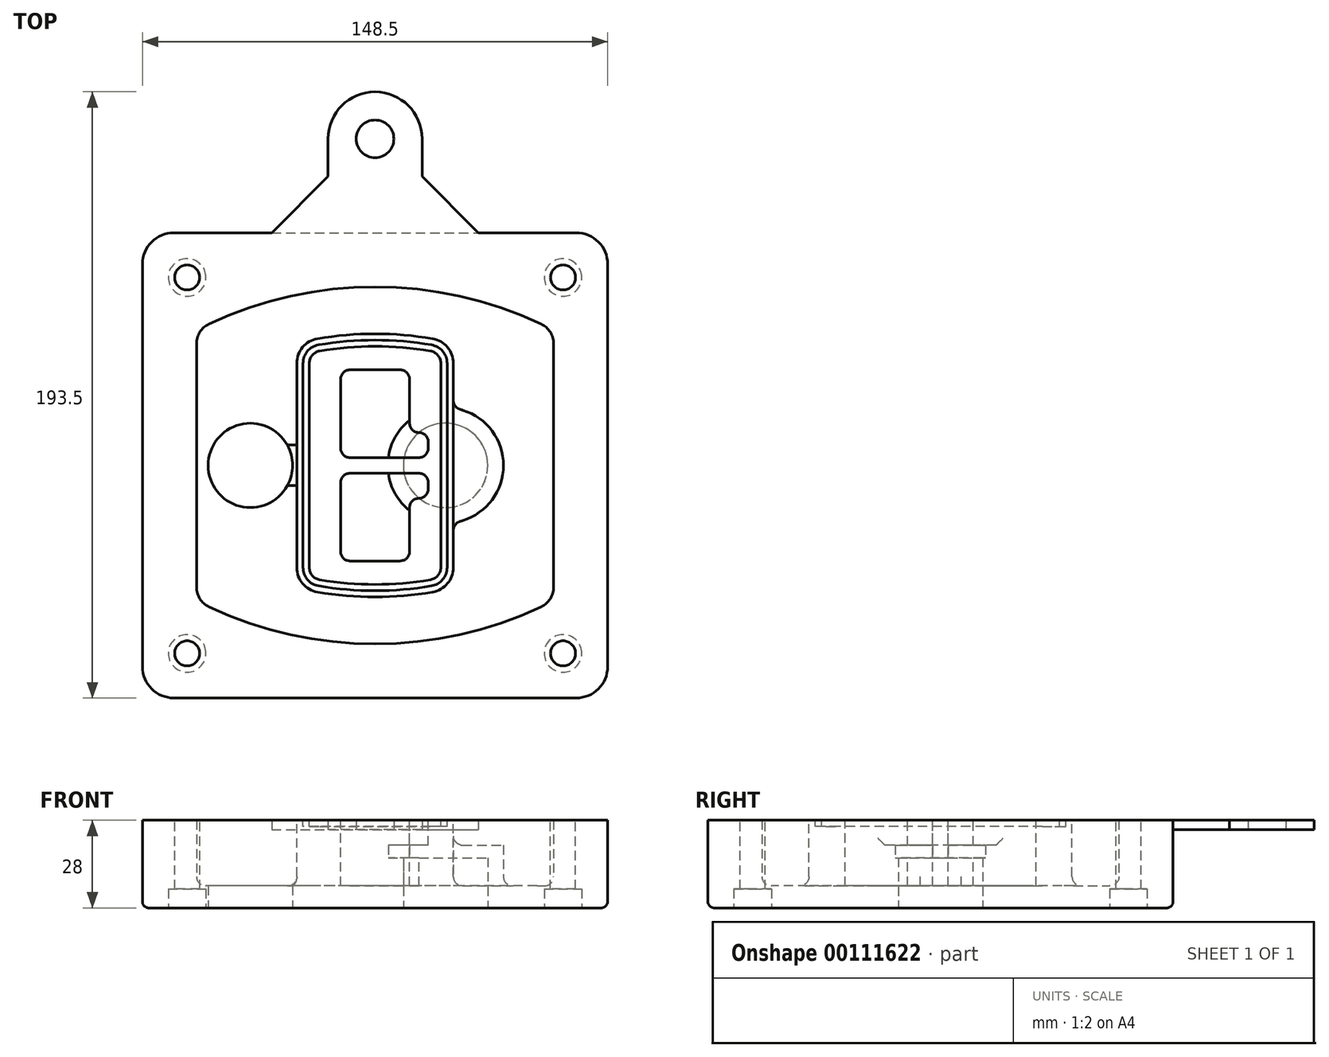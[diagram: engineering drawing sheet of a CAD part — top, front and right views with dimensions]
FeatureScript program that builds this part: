
annotation { "Feature Type Name" : "Feature", "Feature Type Description" : "" }
export const myFeature = defineFeature(function(context is Context, id is Id, definition is map)
    precondition{}
    {
        {
            var Q0;
            Q0=qCreatedBy(makeId("Top.planeOp"),FACE);
            var sketch = newSketch(context, id + "F0", { "sketchPlane" : qUnion([Q0])});
            skPoint(sketch, "E0.rect.middle", {"position": v(0, 0) * mm});
            skLineSegment(sketch, "E1.bottom", {"start": v(-64.25, -74.25) * mm, "end": v(64.25, -74.25) * mm});
            skLineSegment(sketch, "E1.top", {"start": v(-64.25, 74.25) * mm, "end": v(64.25, 74.25) * mm});
            skLineSegment(sketch, "E1.left", {"start": v(-74.25, -64.25) * mm, "end": v(-74.25, 64.25) * mm});
            skLineSegment(sketch, "E1.right", {"start": v(74.25, -64.25) * mm, "end": v(74.25, 64.25) * mm});
            skLineSegment(sketch, "E2", {"start": v(-74.25, 74.25) * mm, "end": v(74.25, -74.25) * mm, "construction": true});
            skLineSegment(sketch, "E3", {"start": v(74.25, 74.25) * mm, "end": v(-74.25, -74.25) * mm, "construction": true});
            skCircle(sketch, "E4", {"center": v(-60, 60) * mm, "radius": 4 * mm});
            skCircle(sketch, "E5", {"center": v(60, 60) * mm, "radius": 4 * mm});
            skCircle(sketch, "E6", {"center": v(60, -60) * mm, "radius": 4 * mm});
            skCircle(sketch, "E7", {"center": v(-60, -60) * mm, "radius": 4 * mm});
            skLineSegment(sketch, "E8", {"start": v(-60, 60) * mm, "end": v(60, 60) * mm, "construction": true});
            skLineSegment(sketch, "E9", {"start": v(60, 60) * mm, "end": v(60, -60) * mm, "construction": true});
            skLineSegment(sketch, "E10", {"start": v(60, -60) * mm, "end": v(-60, -60) * mm, "construction": true});
            skLineSegment(sketch, "E11", {"start": v(-60, -60) * mm, "end": v(-60, 60) * mm, "construction": true});
            skLineSegment(sketch, "E12", {"start": v(-60, 38.83) * mm, "end": v(-60, -38.83) * mm});
            skLineSegment(sketch, "E13", {"start": v(60, 38.83) * mm, "end": v(60, -38.83) * mm});
            skArc(sketch, "E14", {"start": v(54.26, 47.88) * mm, "mid": v(0, 60) * mm, "end": v(-54.26, 47.88) * mm});
            skArc(sketch, "E15", {"start": v(-54.26, -47.88) * mm, "mid": v(0, -60) * mm, "end": v(54.26, -47.88) * mm});
            skLineSegment(sketch, "E16", {"start": v(-60, 0) * mm, "end": v(60, 0) * mm, "construction": true});
            skPoint(sketch, "E17.visualSharp", {"position": v(-60, -45) * mm});
            skArc(sketch, "E17.filletArc", {"start": v(-60, -38.83) * mm, "mid": v(-58.44, -44.2) * mm, "end": v(-54.26, -47.88) * mm});
            skPoint(sketch, "E18.visualSharp", {"position": v(-60, 45) * mm});
            skArc(sketch, "E18.filletArc", {"start": v(-54.26, 47.88) * mm, "mid": v(-58.44, 44.2) * mm, "end": v(-60, 38.83) * mm});
            skPoint(sketch, "E19.visualSharp", {"position": v(60, 45) * mm});
            skArc(sketch, "E19.filletArc", {"start": v(60, 38.83) * mm, "mid": v(58.44, 44.2) * mm, "end": v(54.26, 47.88) * mm});
            skPoint(sketch, "E20.visualSharp", {"position": v(60, -45) * mm});
            skArc(sketch, "E20.filletArc", {"start": v(54.26, -47.88) * mm, "mid": v(58.44, -44.2) * mm, "end": v(60, -38.83) * mm});
            skPoint(sketch, "E21.visualSharp", {"position": v(-74.25, 74.25) * mm});
            skArc(sketch, "E21.filletArc", {"start": v(-64.25, 74.25) * mm, "mid": v(-71.32, 71.32) * mm, "end": v(-74.25, 64.25) * mm});
            skPoint(sketch, "E22.visualSharp", {"position": v(74.25, 74.25) * mm});
            skArc(sketch, "E22.filletArc", {"start": v(74.25, 64.25) * mm, "mid": v(71.32, 71.32) * mm, "end": v(64.25, 74.25) * mm});
            skPoint(sketch, "E23.visualSharp", {"position": v(74.25, -74.25) * mm});
            skArc(sketch, "E23.filletArc", {"start": v(64.25, -74.25) * mm, "mid": v(71.32, -71.32) * mm, "end": v(74.25, -64.25) * mm});
            skPoint(sketch, "E24.visualSharp", {"position": v(-74.25, -74.25) * mm});
            skArc(sketch, "E24.filletArc", {"start": v(-74.25, -64.25) * mm, "mid": v(-71.32, -71.32) * mm, "end": v(-64.25, -74.25) * mm});
            skArc(sketch, "E25.0", {"start": v(57, 38.83) * mm, "mid": v(55.9, 42.58) * mm, "end": v(52.98, 45.17) * mm});
            skLineSegment(sketch, "E25.1", {"start": v(57, 38.83) * mm, "end": v(57, -38.83) * mm});
            skArc(sketch, "E25.2", {"start": v(52.98, -45.17) * mm, "mid": v(55.9, -42.58) * mm, "end": v(57, -38.83) * mm});
            skArc(sketch, "E25.3", {"start": v(-52.98, -45.17) * mm, "mid": v(0, -57) * mm, "end": v(52.98, -45.17) * mm});
            skArc(sketch, "E25.4", {"start": v(-57, -38.83) * mm, "mid": v(-55.9, -42.58) * mm, "end": v(-52.98, -45.17) * mm});
            skArc(sketch, "E25.5", {"start": v(52.98, 45.17) * mm, "mid": v(0, 57) * mm, "end": v(-52.98, 45.17) * mm});
            skLineSegment(sketch, "E25.6", {"start": v(-57, 38.83) * mm, "end": v(-57, -38.83) * mm});
            skArc(sketch, "E25.7", {"start": v(-52.98, 45.17) * mm, "mid": v(-55.9, 42.58) * mm, "end": v(-57, 38.83) * mm});
            skArc(sketch, "E26.0", {"start": v(-55.96, 51.5) * mm, "mid": v(-61.82, 46.33) * mm, "end": v(-64, 38.83) * mm});
            skArc(sketch, "E26.1", {"start": v(55.96, 51.5) * mm, "mid": v(0, 64) * mm, "end": v(-55.96, 51.5) * mm});
            skArc(sketch, "E26.2", {"start": v(64, 38.83) * mm, "mid": v(61.82, 46.33) * mm, "end": v(55.96, 51.5) * mm});
            skLineSegment(sketch, "E26.3", {"start": v(64, 38.83) * mm, "end": v(64, -38.83) * mm});
            skArc(sketch, "E26.4", {"start": v(55.96, -51.5) * mm, "mid": v(61.82, -46.33) * mm, "end": v(64, -38.83) * mm});
            skLineSegment(sketch, "E26.5", {"start": v(-64, 38.83) * mm, "end": v(-64, -38.83) * mm});
            skArc(sketch, "E26.6", {"start": v(-55.96, -51.5) * mm, "mid": v(0, -64) * mm, "end": v(55.96, -51.5) * mm});
            skArc(sketch, "E26.7", {"start": v(-64, -38.83) * mm, "mid": v(-61.82, -46.33) * mm, "end": v(-55.96, -51.5) * mm});
            skSolve(sketch);
        }
        {
            var Q0;
            Q0=makeQuery(id+"F0.imprint","IMPRINT",FACE,{"disambiguationData":[TD([[makeQuery(id+"F0.imprint","IMPRINT",EDGE,{"derivedFrom":sQuery(id+"F0.wireOp",EDGE,"E1.bottom")}),1.0]])]});
            var Q1;
            Q1=makeQuery(id+"F0.imprint","IMPRINT",FACE,{"disambiguationData":[TD([[makeQuery(id+"F0.imprint","IMPRINT",EDGE,{"derivedFrom":sQuery(id+"F0.wireOp",EDGE,"E12")}),1.0]])]});
            var Q2;
            Q2=makeQuery(id+"F0.imprint","IMPRINT",FACE,{"disambiguationData":[TD([[makeQuery(id+"F0.imprint","IMPRINT",EDGE,{"derivedFrom":sQuery(id+"F0.wireOp",EDGE,"E25.0")}),1.0]])]});
            var Q3;
            Q3=makeQuery(id+"F0.imprint","IMPRINT",FACE,{"disambiguationData":[TD([[makeQuery(id+"F0.imprint","IMPRINT",EDGE,{"derivedFrom":sQuery(id+"F0.wireOp",EDGE,"E12")}),-1.0]])]});
            extrude(context, id + "F1", {"entities" : qUnion([Q0, Q1, Q2, Q3]), "oppositeDirection" : true, "depth" : 25 * mm});
        }
        {
            var Q0;
            Q0=makeQuery(id+"F0.imprint","IMPRINT",FACE,{"disambiguationData":[TD([[makeQuery(id+"F0.imprint","IMPRINT",EDGE,{"derivedFrom":sQuery(id+"F0.wireOp",EDGE,"E12")}),1.0]])]});
            extrude(context, id + "F2", {"entities" : qUnion([Q0]), "operationType" : NewBodyOperationType.ADD, "depth" : 3 * mm});
        }
        {
            var Q0;
            Q0=makeQuery(id+"F0.imprint","IMPRINT",FACE,{"disambiguationData":[TD([[makeQuery(id+"F0.imprint","IMPRINT",EDGE,{"derivedFrom":sQuery(id+"F0.wireOp",EDGE,"E25.0")}),1.0]])]});
            extrude(context, id + "F3", {"entities" : qUnion([Q0]), "operationType" : NewBodyOperationType.REMOVE, "oppositeDirection" : true, "depth" : 18 * mm});
        }
        {
            var Q0;
            Q0=makeQuery(id+"F2.opExtrude","CAP_FACE",FACE,{"disambiguationData":[OSD([sQuery(id+"F0.wireOp",EDGE,"E12"),sQuery(id+"F0.wireOp",EDGE,"E13"),sQuery(id+"F0.wireOp",EDGE,"E14"),sQuery(id+"F0.wireOp",EDGE,"E15"),sQuery(id+"F0.wireOp",EDGE,"E17.filletArc"),sQuery(id+"F0.wireOp",EDGE,"E18.filletArc"),sQuery(id+"F0.wireOp",EDGE,"E19.filletArc"),sQuery(id+"F0.wireOp",EDGE,"E20.filletArc"),sQuery(id+"F0.wireOp",EDGE,"E25.0"),sQuery(id+"F0.wireOp",EDGE,"E25.1"),sQuery(id+"F0.wireOp",EDGE,"E25.2"),sQuery(id+"F0.wireOp",EDGE,"E25.3"),sQuery(id+"F0.wireOp",EDGE,"E25.4"),sQuery(id+"F0.wireOp",EDGE,"E25.5"),sQuery(id+"F0.wireOp",EDGE,"E25.6"),sQuery(id+"F0.wireOp",EDGE,"E25.7")])],"isStart":false});
            var sketch = newSketch(context, id + "F4", { "sketchPlane" : qUnion([Q0])});
            skArc(sketch, "E27.0", {"start": v(-18.34, -40.45) * mm, "mid": v(0, -42) * mm, "end": v(18.34, -40.45) * mm});
            skArc(sketch, "E28.0", {"start": v(18.34, 40.45) * mm, "mid": v(0, 42) * mm, "end": v(-18.34, 40.45) * mm});
            skLineSegment(sketch, "E29", {"start": v(-25, 32.57) * mm, "end": v(-25, -32.57) * mm});
            skLineSegment(sketch, "E30", {"start": v(25, 32.57) * mm, "end": v(25, -32.57) * mm});
            skLineSegment(sketch, "E31", {"start": v(-25, 39.1) * mm, "end": v(25, 39.1) * mm, "construction": true});
            skLineSegment(sketch, "E32", {"start": v(-25, -39.1) * mm, "end": v(25, -39.1) * mm, "construction": true});
            skPoint(sketch, "E33.visualSharp", {"position": v(-25, 39.1) * mm});
            skArc(sketch, "E33.filletArc", {"start": v(-18.34, 40.45) * mm, "mid": v(-23.11, 37.73) * mm, "end": v(-25, 32.57) * mm});
            skPoint(sketch, "E34.visualSharp", {"position": v(25, 39.1) * mm});
            skArc(sketch, "E34.filletArc", {"start": v(25, 32.57) * mm, "mid": v(23.11, 37.73) * mm, "end": v(18.34, 40.45) * mm});
            skPoint(sketch, "E35.visualSharp", {"position": v(25, -39.1) * mm});
            skArc(sketch, "E35.filletArc", {"start": v(18.34, -40.45) * mm, "mid": v(23.11, -37.73) * mm, "end": v(25, -32.57) * mm});
            skPoint(sketch, "E36.visualSharp", {"position": v(-25, -39.1) * mm});
            skArc(sketch, "E36.filletArc", {"start": v(-25, -32.57) * mm, "mid": v(-23.11, -37.73) * mm, "end": v(-18.34, -40.45) * mm});
            skArc(sketch, "E37.0", {"start": v(52.98, 45.17) * mm, "mid": v(0, 57) * mm, "end": v(-52.98, 45.17) * mm});
            skArc(sketch, "E37.1", {"start": v(-52.98, 45.17) * mm, "mid": v(-55.9, 42.58) * mm, "end": v(-57, 38.83) * mm});
            skLineSegment(sketch, "E37.2", {"start": v(-57, 38.83) * mm, "end": v(-57, -38.83) * mm});
            skArc(sketch, "E37.3", {"start": v(-57, -38.83) * mm, "mid": v(-55.9, -42.58) * mm, "end": v(-52.98, -45.17) * mm});
            skArc(sketch, "E37.4", {"start": v(-52.98, -45.17) * mm, "mid": v(0, -57) * mm, "end": v(52.98, -45.17) * mm});
            skArc(sketch, "E37.5", {"start": v(52.98, -45.17) * mm, "mid": v(55.9, -42.58) * mm, "end": v(57, -38.83) * mm});
            skLineSegment(sketch, "E37.6", {"start": v(57, 38.83) * mm, "end": v(57, -38.83) * mm});
            skArc(sketch, "E37.7", {"start": v(57, 38.83) * mm, "mid": v(55.9, 42.58) * mm, "end": v(52.98, 45.17) * mm});
            skLineSegment(sketch, "E38.0", {"start": v(23, 32.57) * mm, "end": v(23, -32.57) * mm});
            skArc(sketch, "E38.1", {"start": v(18, -38.48) * mm, "mid": v(21.58, -36.44) * mm, "end": v(23, -32.57) * mm});
            skArc(sketch, "E38.2", {"start": v(-18, -38.48) * mm, "mid": v(0, -40) * mm, "end": v(18, -38.48) * mm});
            skArc(sketch, "E38.3", {"start": v(-23, -32.57) * mm, "mid": v(-21.58, -36.44) * mm, "end": v(-18, -38.48) * mm});
            skLineSegment(sketch, "E38.4", {"start": v(-23, 32.57) * mm, "end": v(-23, -32.57) * mm});
            skArc(sketch, "E38.5", {"start": v(23, 32.57) * mm, "mid": v(21.58, 36.44) * mm, "end": v(18, 38.48) * mm});
            skArc(sketch, "E38.6", {"start": v(-18, 38.48) * mm, "mid": v(-21.58, 36.44) * mm, "end": v(-23, 32.57) * mm});
            skArc(sketch, "E38.7", {"start": v(18, 38.48) * mm, "mid": v(0, 40) * mm, "end": v(-18, 38.48) * mm});
            skArc(sketch, "E39.0", {"start": v(21, 32.57) * mm, "mid": v(20.06, 35.15) * mm, "end": v(17.67, 36.5) * mm});
            skLineSegment(sketch, "E39.1", {"start": v(21, 32.57) * mm, "end": v(21, -32.57) * mm});
            skArc(sketch, "E39.2", {"start": v(17.67, -36.5) * mm, "mid": v(20.06, -35.15) * mm, "end": v(21, -32.57) * mm});
            skArc(sketch, "E39.3", {"start": v(-17.67, -36.5) * mm, "mid": v(0, -38) * mm, "end": v(17.67, -36.5) * mm});
            skArc(sketch, "E39.4", {"start": v(-21, -32.57) * mm, "mid": v(-20.06, -35.15) * mm, "end": v(-17.67, -36.5) * mm});
            skArc(sketch, "E39.5", {"start": v(17.67, 36.5) * mm, "mid": v(0, 38) * mm, "end": v(-17.67, 36.5) * mm});
            skLineSegment(sketch, "E39.6", {"start": v(-21, 32.57) * mm, "end": v(-21, -32.57) * mm});
            skArc(sketch, "E39.7", {"start": v(-17.67, 36.5) * mm, "mid": v(-20.06, 35.15) * mm, "end": v(-21, 32.57) * mm});
            skLineSegment(sketch, "E40", {"start": v(-25, 0) * mm, "end": v(25, 0) * mm, "construction": true});
            skLineSegment(sketch, "E41", {"start": v(-11, 5.5) * mm, "end": v(-11, 27.5) * mm});
            skLineSegment(sketch, "E42", {"start": v(-8, 30.5) * mm, "end": v(8, 30.5) * mm});
            skLineSegment(sketch, "E43", {"start": v(11, 27.5) * mm, "end": v(11, 13.5) * mm});
            skLineSegment(sketch, "E44", {"start": v(14, 10.5) * mm, "end": v(14, 10.5) * mm});
            skLineSegment(sketch, "E45", {"start": v(17, 7.5) * mm, "end": v(17, 5.5) * mm});
            skLineSegment(sketch, "E46", {"start": v(14, 2.5) * mm, "end": v(-8, 2.5) * mm});
            skPoint(sketch, "E47.visualSharp", {"position": v(-11, 30.5) * mm});
            skArc(sketch, "E47.filletArc", {"start": v(-8, 30.5) * mm, "mid": v(-10.12, 29.62) * mm, "end": v(-11, 27.5) * mm});
            skPoint(sketch, "E48.visualSharp", {"position": v(11, 30.5) * mm});
            skArc(sketch, "E48.filletArc", {"start": v(11, 27.5) * mm, "mid": v(10.12, 29.62) * mm, "end": v(8, 30.5) * mm});
            skPoint(sketch, "E49.visualSharp", {"position": v(11, 10.5) * mm});
            skArc(sketch, "E49.filletArc", {"start": v(11, 13.5) * mm, "mid": v(11.88, 11.38) * mm, "end": v(14, 10.5) * mm});
            skPoint(sketch, "E50.visualSharp", {"position": v(17, 10.5) * mm});
            skArc(sketch, "E50.filletArc", {"start": v(17, 7.5) * mm, "mid": v(16.12, 9.62) * mm, "end": v(14, 10.5) * mm});
            skPoint(sketch, "E51.visualSharp", {"position": v(17, 2.5) * mm});
            skArc(sketch, "E51.filletArc", {"start": v(14, 2.5) * mm, "mid": v(16.12, 3.38) * mm, "end": v(17, 5.5) * mm});
            skPoint(sketch, "E52.visualSharp", {"position": v(-11, 2.5) * mm});
            skArc(sketch, "E52.filletArc", {"start": v(-11, 5.5) * mm, "mid": v(-10.12, 3.38) * mm, "end": v(-8, 2.5) * mm});
            skLineSegment(sketch, "E53.0.MirrorCS", {"start": v(14, -2.5) * mm, "end": v(-8, -2.5) * mm});
            skArc(sketch, "E54.0.MirrorCS", {"start": v(-11, -5.5) * mm, "mid": v(-10.12, -3.38) * mm, "end": v(-8, -2.5) * mm});
            skLineSegment(sketch, "E55.0.MirrorCS", {"start": v(-11, -5.5) * mm, "end": v(-11, -27.5) * mm});
            skArc(sketch, "E56.0.MirrorCS", {"start": v(-8, -30.5) * mm, "mid": v(-10.12, -29.62) * mm, "end": v(-11, -27.5) * mm});
            skLineSegment(sketch, "E57.0.MirrorCS", {"start": v(-8, -30.5) * mm, "end": v(8, -30.5) * mm});
            skArc(sketch, "E58.0.MirrorCS", {"start": v(11, -27.5) * mm, "mid": v(10.12, -29.62) * mm, "end": v(8, -30.5) * mm});
            skLineSegment(sketch, "E59.0.MirrorCS", {"start": v(11, -27.5) * mm, "end": v(11, -13.5) * mm});
            skArc(sketch, "E60.0.MirrorCS", {"start": v(11, -13.5) * mm, "mid": v(11.88, -11.38) * mm, "end": v(14, -10.5) * mm});
            skArc(sketch, "E61.0.MirrorCS", {"start": v(17, -7.5) * mm, "mid": v(16.12, -9.62) * mm, "end": v(14, -10.5) * mm});
            skLineSegment(sketch, "E62.0.MirrorCS", {"start": v(17, -7.5) * mm, "end": v(17, -5.5) * mm});
            skArc(sketch, "E63.0.MirrorCS", {"start": v(14, -2.5) * mm, "mid": v(16.12, -3.38) * mm, "end": v(17, -5.5) * mm});
            skSolve(sketch);
        }
        {
            var Q0;
            Q0=makeQuery(id+"F4.imprint","IMPRINT",FACE,{"disambiguationData":[TD([[makeQuery(id+"F4.imprint","IMPRINT",EDGE,{"derivedFrom":sQuery(id+"F4.wireOp",EDGE,"E27.0")}),1.0]])]});
            var Q1;
            Q1=makeQuery(id+"F4.imprint","IMPRINT",FACE,{"disambiguationData":[TD([[makeQuery(id+"F4.imprint","IMPRINT",EDGE,{"derivedFrom":sQuery(id+"F4.wireOp",EDGE,"E38.0")}),-1.0]])]});
            var Q2;
            Q2=makeQuery(id+"F4.imprint","IMPRINT",FACE,{"disambiguationData":[TD([[makeQuery(id+"F4.imprint","IMPRINT",EDGE,{"derivedFrom":sQuery(id+"F4.wireOp",EDGE,"E39.0")}),1.0]])]});
            extrude(context, id + "F5", {"entities" : qUnion([Q0, Q1, Q2]), "operationType" : NewBodyOperationType.ADD, "endBound" : BoundingType.UP_TO_NEXT, "oppositeDirection" : true, "depth" : 25 * mm});
        }
        {
            var Q0;
            Q0=makeQuery(id+"F4.imprint","IMPRINT",FACE,{"disambiguationData":[TD([[makeQuery(id+"F4.imprint","IMPRINT",EDGE,{"derivedFrom":sQuery(id+"F4.wireOp",EDGE,"E38.0")}),-1.0]])]});
            extrude(context, id + "F6", {"entities" : qUnion([Q0]), "operationType" : NewBodyOperationType.REMOVE, "oppositeDirection" : true, "depth" : 2 * mm});
        }
        {
            var Q0;
            Q0=makeQuery(id+"F1.opExtrude","CAP_FACE",FACE,{"disambiguationData":[OSD([sQuery(id+"F0.wireOp",EDGE,"E1.bottom"),sQuery(id+"F0.wireOp",EDGE,"E1.top"),sQuery(id+"F0.wireOp",EDGE,"E1.left"),sQuery(id+"F0.wireOp",EDGE,"E1.right"),sQuery(id+"F0.wireOp",EDGE,"E4"),sQuery(id+"F0.wireOp",EDGE,"E5"),sQuery(id+"F0.wireOp",EDGE,"E6"),sQuery(id+"F0.wireOp",EDGE,"E7"),sQuery(id+"F0.wireOp",EDGE,"E21.filletArc"),sQuery(id+"F0.wireOp",EDGE,"E22.filletArc"),sQuery(id+"F0.wireOp",EDGE,"E23.filletArc"),sQuery(id+"F0.wireOp",EDGE,"E24.filletArc")])],"isStart":false});
            var sketch = newSketch(context, id + "F7", { "sketchPlane" : qUnion([Q0])});
            skCircle(sketch, "E64", {"center": v(22.5, 0) * mm, "radius": 13.47 * mm});
            skCircle(sketch, "E65", {"center": v(-39.81, 0) * mm, "radius": 13.47 * mm});
            skLineSegment(sketch, "E66", {"start": v(74.25, 0) * mm, "end": v(-74.25, 0) * mm});
            skCircle(sketch, "E67", {"center": v(22.5, 0) * mm, "radius": 18.47 * mm});
            skCircle(sketch, "E68", {"center": v(60, -60) * mm, "radius": 6 * mm});
            skCircle(sketch, "E69", {"center": v(-60, -60) * mm, "radius": 6 * mm});
            skCircle(sketch, "E70", {"center": v(-60, 60) * mm, "radius": 6 * mm});
            skCircle(sketch, "E71", {"center": v(60, 60) * mm, "radius": 6 * mm});
            skSolve(sketch);
        }
        {
            var Q0;
            {var subQ1=sQuery(id+"F7.wireOp",EDGE,"E66");var subQ4=sQuery(id+"F7.wireOp",EDGE,"E64");var subQ6=makeQuery(id+"F7.imprint","INTERSECT",VERTEX,{"disambiguationData":[OD(0.0)],"derivedFrom":[subQ4,subQ1]});Q0=makeQuery(id+"F7.imprint","IMPRINT",FACE,{"disambiguationData":[TD([[makeQuery(id+"F7.imprint","IMPRINT",EDGE,{"disambiguationData":[TD([[subQ6,-1.0]])],"derivedFrom":subQ4}),-1.0]])]});}
            var Q1;
            {var subQ0=sQuery(id+"F7.wireOp",EDGE,"E66");var subQ1=sQuery(id+"F7.wireOp",EDGE,"E64");var subQ3=makeQuery(id+"F7.imprint","INTERSECT",VERTEX,{"disambiguationData":[OD(0.0)],"derivedFrom":[subQ1,subQ0]});Q1=makeQuery(id+"F7.imprint","IMPRINT",FACE,{"disambiguationData":[TD([[makeQuery(id+"F7.imprint","IMPRINT",EDGE,{"disambiguationData":[TD([[subQ3,-1.0]])],"derivedFrom":subQ1}),1.0]])]});}
            var Q2;
            {var subQ0=sQuery(id+"F7.wireOp",EDGE,"E66");var subQ1=sQuery(id+"F7.wireOp",EDGE,"E64");var subQ3=makeQuery(id+"F7.imprint","INTERSECT",VERTEX,{"disambiguationData":[OD(0.0)],"derivedFrom":[subQ1,subQ0]});Q2=makeQuery(id+"F7.imprint","IMPRINT",FACE,{"disambiguationData":[TD([[makeQuery(id+"F7.imprint","IMPRINT",EDGE,{"disambiguationData":[TD([[subQ3,1.0]])],"derivedFrom":subQ1}),1.0]])]});}
            var Q3;
            {var subQ1=sQuery(id+"F7.wireOp",EDGE,"E66");var subQ4=sQuery(id+"F7.wireOp",EDGE,"E64");var subQ6=makeQuery(id+"F7.imprint","INTERSECT",VERTEX,{"disambiguationData":[OD(0.0)],"derivedFrom":[subQ4,subQ1]});Q3=makeQuery(id+"F7.imprint","IMPRINT",FACE,{"disambiguationData":[TD([[makeQuery(id+"F7.imprint","IMPRINT",EDGE,{"disambiguationData":[TD([[subQ6,1.0]])],"derivedFrom":subQ4}),-1.0]])]});}
            extrude(context, id + "F8", {"entities" : qUnion([Q0, Q1, Q2, Q3]), "operationType" : NewBodyOperationType.ADD, "oppositeDirection" : true, "depth" : 20 * mm});
        }
        {
            var Q0;
            {var subQ0=sQuery(id+"F7.wireOp",EDGE,"E66");var subQ1=sQuery(id+"F7.wireOp",EDGE,"E64");var subQ3=makeQuery(id+"F7.imprint","INTERSECT",VERTEX,{"disambiguationData":[OD(0.0)],"derivedFrom":[subQ1,subQ0]});Q0=makeQuery(id+"F7.imprint","IMPRINT",FACE,{"disambiguationData":[TD([[makeQuery(id+"F7.imprint","IMPRINT",EDGE,{"disambiguationData":[TD([[subQ3,-1.0]])],"derivedFrom":subQ1}),1.0]])]});}
            var Q1;
            {var subQ0=sQuery(id+"F7.wireOp",EDGE,"E66");var subQ1=sQuery(id+"F7.wireOp",EDGE,"E64");var subQ3=makeQuery(id+"F7.imprint","INTERSECT",VERTEX,{"disambiguationData":[OD(0.0)],"derivedFrom":[subQ1,subQ0]});Q1=makeQuery(id+"F7.imprint","IMPRINT",FACE,{"disambiguationData":[TD([[makeQuery(id+"F7.imprint","IMPRINT",EDGE,{"disambiguationData":[TD([[subQ3,1.0]])],"derivedFrom":subQ1}),1.0]])]});}
            extrude(context, id + "F9", {"entities" : qUnion([Q0, Q1]), "operationType" : NewBodyOperationType.REMOVE, "oppositeDirection" : true, "depth" : 16 * mm});
        }
        {
            var Q0;
            {var subQ0=sQuery(id+"F7.wireOp",EDGE,"E66");var subQ1=sQuery(id+"F7.wireOp",EDGE,"E65");var subQ3=makeQuery(id+"F7.imprint","INTERSECT",VERTEX,{"disambiguationData":[OD(0.0)],"derivedFrom":[subQ1,subQ0]});Q0=makeQuery(id+"F7.imprint","IMPRINT",FACE,{"disambiguationData":[TD([[makeQuery(id+"F7.imprint","IMPRINT",EDGE,{"disambiguationData":[TD([[subQ3,-1.0]])],"derivedFrom":subQ1}),1.0]])]});}
            var Q1;
            {var subQ0=sQuery(id+"F7.wireOp",EDGE,"E66");var subQ1=sQuery(id+"F7.wireOp",EDGE,"E65");var subQ3=makeQuery(id+"F7.imprint","INTERSECT",VERTEX,{"disambiguationData":[OD(0.0)],"derivedFrom":[subQ1,subQ0]});Q1=makeQuery(id+"F7.imprint","IMPRINT",FACE,{"disambiguationData":[TD([[makeQuery(id+"F7.imprint","IMPRINT",EDGE,{"disambiguationData":[TD([[subQ3,1.0]])],"derivedFrom":subQ1}),1.0]])]});}
            extrude(context, id + "F10", {"entities" : qUnion([Q0, Q1]), "operationType" : NewBodyOperationType.REMOVE, "oppositeDirection" : true, "depth" : 25 * mm});
        }
        {
            var Q0;
            Q0=makeQuery(id+"F7.imprint","IMPRINT",FACE,{"disambiguationData":[TD([[makeQuery(id+"F7.imprint","IMPRINT",EDGE,{"derivedFrom":sQuery(id+"F7.wireOp",EDGE,"E68")}),1.0]])]});
            var Q1;
            Q1=makeQuery(id+"F7.imprint","IMPRINT",FACE,{"disambiguationData":[TD([[makeQuery(id+"F7.imprint","IMPRINT",EDGE,{"derivedFrom":makeQuery(id+"F1.opExtrude","CAP_EDGE",EDGE,{"disambiguationData":[OSD([sQuery(id+"F0.wireOp",EDGE,"E5")])],"isStart":false})}),-1.0]])]});
            var Q2;
            Q2=makeQuery(id+"F7.imprint","IMPRINT",FACE,{"disambiguationData":[TD([[makeQuery(id+"F7.imprint","IMPRINT",EDGE,{"derivedFrom":sQuery(id+"F7.wireOp",EDGE,"E69")}),1.0]])]});
            var Q3;
            Q3=makeQuery(id+"F7.imprint","IMPRINT",FACE,{"disambiguationData":[TD([[makeQuery(id+"F7.imprint","IMPRINT",EDGE,{"derivedFrom":makeQuery(id+"F1.opExtrude","CAP_EDGE",EDGE,{"disambiguationData":[OSD([sQuery(id+"F0.wireOp",EDGE,"E4")])],"isStart":false})}),-1.0]])]});
            var Q4;
            Q4=makeQuery(id+"F7.imprint","IMPRINT",FACE,{"disambiguationData":[TD([[makeQuery(id+"F7.imprint","IMPRINT",EDGE,{"derivedFrom":sQuery(id+"F7.wireOp",EDGE,"E70")}),1.0]])]});
            var Q5;
            Q5=makeQuery(id+"F7.imprint","IMPRINT",FACE,{"disambiguationData":[TD([[makeQuery(id+"F7.imprint","IMPRINT",EDGE,{"derivedFrom":makeQuery(id+"F1.opExtrude","CAP_EDGE",EDGE,{"disambiguationData":[OSD([sQuery(id+"F0.wireOp",EDGE,"E7")])],"isStart":false})}),-1.0]])]});
            var Q6;
            Q6=makeQuery(id+"F7.imprint","IMPRINT",FACE,{"disambiguationData":[TD([[makeQuery(id+"F7.imprint","IMPRINT",EDGE,{"derivedFrom":sQuery(id+"F7.wireOp",EDGE,"E71")}),1.0]])]});
            var Q7;
            Q7=makeQuery(id+"F7.imprint","IMPRINT",FACE,{"disambiguationData":[TD([[makeQuery(id+"F7.imprint","IMPRINT",EDGE,{"derivedFrom":makeQuery(id+"F1.opExtrude","CAP_EDGE",EDGE,{"disambiguationData":[OSD([sQuery(id+"F0.wireOp",EDGE,"E6")])],"isStart":false})}),-1.0]])]});
            extrude(context, id + "F11", {"entities" : qUnion([Q0, Q1, Q2, Q3, Q4, Q5, Q6, Q7]), "operationType" : NewBodyOperationType.REMOVE, "oppositeDirection" : true, "depth" : 6 * mm});
        }
        {
            var Q0;
            Q0=makeQuery(id+"F9.boolean.opBoolean","COPY",FACE,{"derivedFrom":makeQuery(id+"F9.opExtrude","CAP_FACE",FACE,{"disambiguationData":[OSD([sQuery(id+"F7.wireOp",EDGE,"E64")])],"isStart":false})});
            var sketch = newSketch(context, id + "F12", { "sketchPlane" : qUnion([Q0])});
            skArc(sketch, "E72.0", {"start": v(11, 14.45) * mm, "mid": v(6.45, 9.13) * mm, "end": v(4.2, 2.5) * mm});
            skArc(sketch, "E72.1", {"start": v(4.2, -2.5) * mm, "mid": v(6.45, -9.13) * mm, "end": v(11, -14.45) * mm});
            skLineSegment(sketch, "E73", {"start": v(4.2, -2.5) * mm, "end": v(14, -2.5) * mm});
            skLineSegment(sketch, "E74.0", {"start": v(14, 2.5) * mm, "end": v(4.2, 2.5) * mm});
            skArc(sketch, "E74.1", {"start": v(14, 2.5) * mm, "mid": v(16.12, 3.38) * mm, "end": v(17, 5.5) * mm});
            skLineSegment(sketch, "E74.2", {"start": v(17, 7.5) * mm, "end": v(17, 5.5) * mm});
            skArc(sketch, "E74.3", {"start": v(17, 7.5) * mm, "mid": v(16.12, 9.62) * mm, "end": v(14, 10.5) * mm});
            skArc(sketch, "E74.4", {"start": v(11, 13.5) * mm, "mid": v(11.88, 11.38) * mm, "end": v(14, 10.5) * mm});
            skLineSegment(sketch, "E74.5", {"start": v(11, 14.45) * mm, "end": v(11, 13.5) * mm});
            skLineSegment(sketch, "E74.7", {"start": v(14, -2.5) * mm, "end": v(4.2, -2.5) * mm});
            skArc(sketch, "E74.8", {"start": v(14, -2.5) * mm, "mid": v(16.12, -3.38) * mm, "end": v(17, -5.5) * mm});
            skLineSegment(sketch, "E74.9", {"start": v(17, -7.5) * mm, "end": v(17, -5.5) * mm});
            skArc(sketch, "E74.10", {"start": v(17, -7.5) * mm, "mid": v(16.12, -9.62) * mm, "end": v(14, -10.5) * mm});
            skArc(sketch, "E74.11", {"start": v(11, -13.5) * mm, "mid": v(11.88, -11.38) * mm, "end": v(14, -10.5) * mm});
            skLineSegment(sketch, "E74.12", {"start": v(11, -14.45) * mm, "end": v(11, -13.5) * mm});
            skPoint(sketch, "E75.orphan", {"position": v(11, -27.5) * mm});
            skPoint(sketch, "E76.orphan", {"position": v(-8, -2.5) * mm});
            skPoint(sketch, "E77.orphan", {"position": v(-8, 2.5) * mm});
            skPoint(sketch, "E78.orphan", {"position": v(11, 27.5) * mm});
            skSolve(sketch);
        }
        {
            var Q0;
            {var subQ7=sQuery(id+"F12.wireOp",EDGE,"E72.0");var subQ14=sQuery(id+"F12.wireOp",EDGE,"E72.1");var subQ16=sQuery(id+"F12.wireOp",EDGE,"E74.1");var subQ18=sQuery(id+"F12.wireOp",EDGE,"E74.8");Q0=qUnion([makeQuery(id+"F12.imprint","IMPRINT",FACE,{"disambiguationData":[TD([[makeQuery(id+"F12.imprint","IMPRINT",EDGE,{"derivedFrom":subQ7}),1.0]])]}),makeQuery(id+"F12.imprint","IMPRINT",FACE,{"disambiguationData":[TD([[makeQuery(id+"F12.imprint","IMPRINT",EDGE,{"derivedFrom":subQ14}),1.0]])]}),makeQuery(id+"F12.imprint","IMPRINT",FACE,{"disambiguationData":[TD([[makeQuery(id+"F12.imprint","IMPRINT",EDGE,{"derivedFrom":subQ16}),1.0]])]}),makeQuery(id+"F12.imprint","IMPRINT",FACE,{"disambiguationData":[TD([[makeQuery(id+"F12.imprint","IMPRINT",EDGE,{"derivedFrom":subQ18}),-1.0]])]})]);}
            var Q1;
            Q1=makeQuery(id+"F5.boolean.opBoolean","SPLIT",FACE,{"disambiguationData":[TD([makeQuery(id+"F5.opExtrude","SWEPT_FACE",FACE,{"disambiguationData":[OSD([sQuery(id+"F4.wireOp",EDGE,"E41")])]})])],"derivedFrom":makeQuery(id+"F3.boolean.opBoolean","COPY",FACE,{"derivedFrom":makeQuery(id+"F3.opExtrude","CAP_FACE",FACE,{"disambiguationData":[OSD([sQuery(id+"F0.wireOp",EDGE,"E25.0"),sQuery(id+"F0.wireOp",EDGE,"E25.1"),sQuery(id+"F0.wireOp",EDGE,"E25.2"),sQuery(id+"F0.wireOp",EDGE,"E25.3"),sQuery(id+"F0.wireOp",EDGE,"E25.4"),sQuery(id+"F0.wireOp",EDGE,"E25.5"),sQuery(id+"F0.wireOp",EDGE,"E25.6"),sQuery(id+"F0.wireOp",EDGE,"E25.7")])],"isStart":false})})});
            extrude(context, id + "F13", {"entities" : qUnion([Q0]), "operationType" : NewBodyOperationType.REMOVE, "endBound" : BoundingType.UP_TO_SURFACE, "endBoundEntityFace" : qUnion([Q1]), "depth" : 25 * mm});
        }
        {
            var Q0;
            Q0=makeQuery(id+"F3.boolean.opBoolean","COPY",EDGE,{"derivedFrom":makeQuery(id+"F3.opExtrude","CAP_EDGE",EDGE,{"disambiguationData":[OSD([sQuery(id+"F0.wireOp",EDGE,"E25.6")])],"isStart":false})});
            var Q1;
            Q1=makeQuery(id+"F8.boolean.opBoolean","INTERSECT",EDGE,{"derivedFrom":[makeQuery(id+"F5.opExtrude","SWEPT_FACE",FACE,{"disambiguationData":[OSD([sQuery(id+"F4.wireOp",EDGE,"E30")])]}),makeQuery(id+"F8.opExtrude","CAP_FACE",FACE,{"disambiguationData":[OSD([sQuery(id+"F7.wireOp",EDGE,"E67")])],"isStart":false})]});
            var Q2;
            Q2=makeQuery(id+"F8.boolean.opBoolean","INTERSECT",EDGE,{"disambiguationData":[OD(1.0)],"derivedFrom":[makeQuery(id+"F5.opExtrude","SWEPT_FACE",FACE,{"disambiguationData":[OSD([sQuery(id+"F4.wireOp",EDGE,"E30")])]}),makeQuery(id+"F8.opExtrude","SWEPT_FACE",FACE,{"disambiguationData":[OSD([sQuery(id+"F7.wireOp",EDGE,"E67")])]})]});
            var Q3;
            {var subQ0=sQuery(id+"F4.wireOp",EDGE,"E30");Q3=makeQuery(id+"F8.boolean.opBoolean","SPLIT",EDGE,{"disambiguationData":[TD([makeQuery(id+"F5.opExtrude","SWEPT_FACE",FACE,{"disambiguationData":[OSD([sQuery(id+"F4.wireOp",EDGE,"E35.filletArc")])]})])],"derivedFrom":makeQuery(id+"F5.opExtrude","CAP_EDGE",EDGE,{"disambiguationData":[OSD([subQ0])],"isStart":false})});}
            var Q4;
            {var subQ0=sQuery(id+"F0.wireOp",EDGE,"E25.7");var subQ1=sQuery(id+"F0.wireOp",EDGE,"E25.1");var subQ2=sQuery(id+"F0.wireOp",EDGE,"E25.6");var subQ3=sQuery(id+"F0.wireOp",EDGE,"E25.5");var subQ4=sQuery(id+"F0.wireOp",EDGE,"E25.4");var subQ5=sQuery(id+"F0.wireOp",EDGE,"E25.0");var subQ6=sQuery(id+"F0.wireOp",EDGE,"E25.2");var subQ7=sQuery(id+"F0.wireOp",EDGE,"E25.3");Q4=makeQuery(id+"F8.boolean.opBoolean","INTERSECT",EDGE,{"derivedFrom":[makeQuery(id+"F5.boolean.opBoolean","SPLIT",FACE,{"disambiguationData":[TD([makeQuery(id+"F2.opExtrude","SWEPT_FACE",FACE,{"disambiguationData":[OSD([subQ5])]})])],"derivedFrom":makeQuery(id+"F3.boolean.opBoolean","COPY",FACE,{"derivedFrom":makeQuery(id+"F3.opExtrude","CAP_FACE",FACE,{"disambiguationData":[OSD([subQ5,subQ1,subQ6,subQ7,subQ4,subQ3,subQ2,subQ0])],"isStart":false})})}),makeQuery(id+"F8.opExtrude","SWEPT_FACE",FACE,{"disambiguationData":[OSD([sQuery(id+"F7.wireOp",EDGE,"E67")])]})]});}
            var Q5;
            Q5=makeQuery(id+"F8.boolean.opBoolean","INTERSECT",EDGE,{"disambiguationData":[OD(0.0)],"derivedFrom":[makeQuery(id+"F5.opExtrude","SWEPT_FACE",FACE,{"disambiguationData":[OSD([sQuery(id+"F4.wireOp",EDGE,"E30")])]}),makeQuery(id+"F8.opExtrude","SWEPT_FACE",FACE,{"disambiguationData":[OSD([sQuery(id+"F7.wireOp",EDGE,"E67")])]})]});
            fillet(context, id + "F14", {"entities" : qUnion([Q0, Q1, Q2, Q3, Q4, Q5]), "radius" : 3 * mm, "tangentPropagation" : true, "allowEdgeOverflow" : false});
        }
        {
            var Q0;
            Q0=makeQuery(id+"F1.opExtrude","CAP_EDGE",EDGE,{"disambiguationData":[OSD([sQuery(id+"F0.wireOp",EDGE,"E1.bottom")])],"isStart":false});
            fillet(context, id + "F15", {"entities" : qUnion([Q0]), "radius" : 2 * mm, "tangentPropagation" : true, "allowEdgeOverflow" : false});
        }
        {
            var Q0;
            {var subQ0=sQuery(id+"F0.wireOp",EDGE,"E22.filletArc");var subQ1=sQuery(id+"F0.wireOp",EDGE,"E7");var subQ2=sQuery(id+"F0.wireOp",EDGE,"E6");var subQ3=sQuery(id+"F0.wireOp",EDGE,"E5");var subQ4=sQuery(id+"F0.wireOp",EDGE,"E4");var subQ5=sQuery(id+"F0.wireOp",EDGE,"E1.bottom");var subQ6=sQuery(id+"F0.wireOp",EDGE,"E21.filletArc");var subQ7=sQuery(id+"F0.wireOp",EDGE,"E1.top");var subQ8=sQuery(id+"F0.wireOp",EDGE,"E1.left");var subQ9=sQuery(id+"F0.wireOp",EDGE,"E1.right");var subQ10=sQuery(id+"F0.wireOp",EDGE,"E23.filletArc");var subQ11=sQuery(id+"F0.wireOp",EDGE,"E24.filletArc");Q0=makeQuery(id+"F2.boolean.opBoolean","SPLIT",FACE,{"disambiguationData":[TD([makeQuery(id+"F1.opExtrude","SWEPT_FACE",FACE,{"disambiguationData":[OSD([subQ5])]})])],"derivedFrom":makeQuery(id+"F1.opExtrude","CAP_FACE",FACE,{"disambiguationData":[OSD([subQ5,subQ7,subQ8,subQ9,subQ4,subQ3,subQ2,subQ1,subQ6,subQ0,subQ10,subQ11])],"isStart":true})});}
            var sketch = newSketch(context, id + "F16", { "sketchPlane" : qUnion([Q0])});
            skLineSegment(sketch, "E79", {"start": v(0, 74.25) * mm, "end": v(0, 104.25) * mm, "construction": true});
            skPoint(sketch, "E79.endSnap0", {"position": v(0, 74.25) * mm});
            skLineSegment(sketch, "E80", {"start": v(-33, 74.25) * mm, "end": v(-15, 92.25) * mm});
            skLineSegment(sketch, "E81", {"start": v(-15, 92.25) * mm, "end": v(-15, 104.25) * mm});
            skArc(sketch, "E82", {"start": v(15, 104.25) * mm, "mid": v(0, 119.25) * mm, "end": v(-15, 104.25) * mm});
            skLineSegment(sketch, "E83", {"start": v(15, 104.25) * mm, "end": v(15, 92.25) * mm});
            skLineSegment(sketch, "E84", {"start": v(15, 92.25) * mm, "end": v(33, 74.25) * mm});
            skCircle(sketch, "E85", {"center": v(0, 104.25) * mm, "radius": 6 * mm});
            skLineSegment(sketch, "E86", {"start": v(-70.78, 0) * mm, "end": v(74.25, 0) * mm, "construction": true});
            skPoint(sketch, "E86.startSnap0", {"position": v(-74.25, 0) * mm});
            skArc(sketch, "E87.MirrorCS", {"start": v(15, -104.25) * mm, "mid": v(0, -119.25) * mm, "end": v(-15, -104.25) * mm});
            skLineSegment(sketch, "E88.MirrorCS", {"start": v(-15, -92.25) * mm, "end": v(-15, -104.25) * mm});
            skLineSegment(sketch, "E89.MirrorCS", {"start": v(15, -104.25) * mm, "end": v(15, -92.25) * mm});
            skLineSegment(sketch, "E90.MirrorCS", {"start": v(15, -92.25) * mm, "end": v(33, -74.25) * mm});
            skLineSegment(sketch, "E91.MirrorCS", {"start": v(-33, -74.25) * mm, "end": v(-15, -92.25) * mm});
            skLineSegment(sketch, "E92.MirrorCS", {"start": v(0, -74.25) * mm, "end": v(0, -104.25) * mm, "construction": true});
            skCircle(sketch, "E93.MirrorC", {"center": v(0, -104.25) * mm, "radius": 6 * mm});
            skSolve(sketch);
        }
        {
            var Q0;
            Q0=makeQuery(id+"F16.imprint","IMPRINT",FACE,{"disambiguationData":[TD([[makeQuery(id+"F16.imprint","IMPRINT",EDGE,{"derivedFrom":makeQuery(id+"F1.opExtrude","CAP_EDGE",EDGE,{"disambiguationData":[OSD([sQuery(id+"F0.wireOp",EDGE,"E1.left")])],"isStart":true})}),-1.0]])]});
            var Q1;
            {var subQ0=sQuery(id+"F16.wireOp",EDGE,"E80");Q1=makeQuery(id+"F16.imprint","IMPRINT",FACE,{"disambiguationData":[TD([[makeQuery(id+"F16.imprint","IMPRINT",EDGE,{"derivedFrom":subQ0}),-1.0]])]});}
            var Q2;
            Q2=makeQuery(id+"F16.imprint","IMPRINT",FACE,{"disambiguationData":[TD([[makeQuery(id+"F16.imprint","IMPRINT",EDGE,{"derivedFrom":sQuery(id+"F16.wireOp",EDGE,"E87.MirrorCS")}),-1.0]])]});
            var Q3;
            Q3=makeQuery(id+"F2.opExtrude","CAP_FACE",FACE,{"disambiguationData":[OSD([sQuery(id+"F0.wireOp",EDGE,"E12"),sQuery(id+"F0.wireOp",EDGE,"E13"),sQuery(id+"F0.wireOp",EDGE,"E14"),sQuery(id+"F0.wireOp",EDGE,"E15"),sQuery(id+"F0.wireOp",EDGE,"E17.filletArc"),sQuery(id+"F0.wireOp",EDGE,"E18.filletArc"),sQuery(id+"F0.wireOp",EDGE,"E19.filletArc"),sQuery(id+"F0.wireOp",EDGE,"E20.filletArc"),sQuery(id+"F0.wireOp",EDGE,"E25.0"),sQuery(id+"F0.wireOp",EDGE,"E25.1"),sQuery(id+"F0.wireOp",EDGE,"E25.2"),sQuery(id+"F0.wireOp",EDGE,"E25.3"),sQuery(id+"F0.wireOp",EDGE,"E25.4"),sQuery(id+"F0.wireOp",EDGE,"E25.5"),sQuery(id+"F0.wireOp",EDGE,"E25.6"),sQuery(id+"F0.wireOp",EDGE,"E25.7")])],"isStart":false});
            extrude(context, id + "F17", {"entities" : qUnion([Q0, Q1, Q2]), "operationType" : NewBodyOperationType.ADD, "endBound" : BoundingType.UP_TO_SURFACE, "endBoundEntityFace" : qUnion([Q3]), "depth" : 25 * mm});
        }
    });
